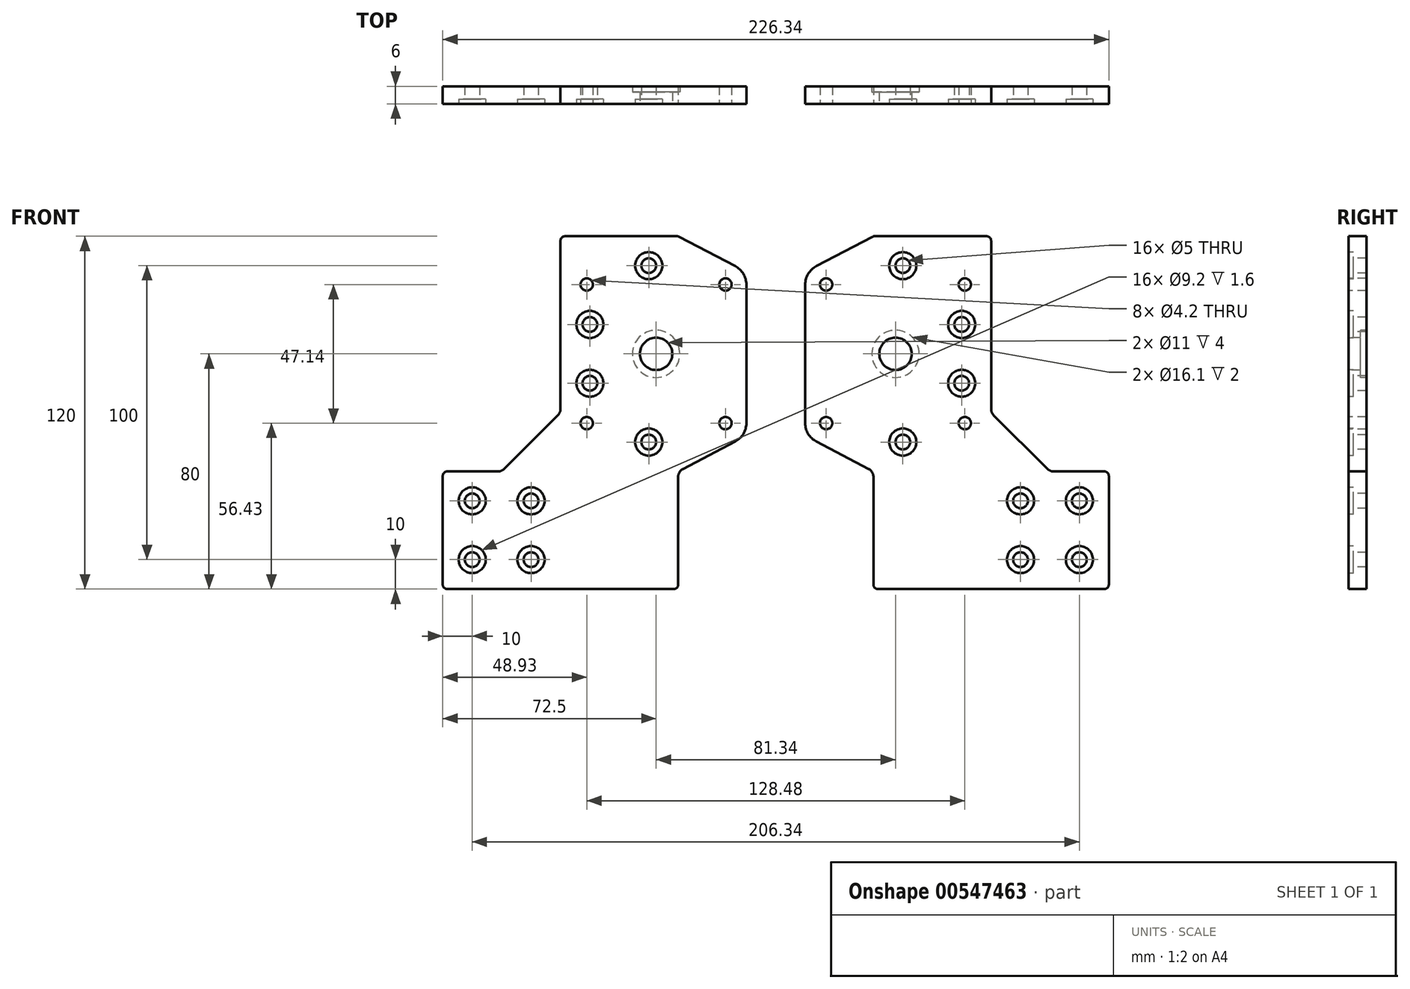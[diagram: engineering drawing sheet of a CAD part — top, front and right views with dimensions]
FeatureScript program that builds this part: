
annotation { "Feature Type Name" : "Feature", "Feature Type Description" : "" }
export const myFeature = defineFeature(function(context is Context, id is Id, definition is map)
    precondition{}
    {
        {
            var Q0;
            Q0=qCreatedBy(makeId("Front.planeOp"),FACE);
            var sketch = newSketch(context, id + "F0", { "sketchPlane" : qUnion([Q0])});
            skCircle(sketch, "E0", {"center": v(-80, -70) * mm, "radius": 2.5 * mm});
            skCircle(sketch, "E1", {"center": v(-80, -70) * mm, "radius": 4.6 * mm});
            skCircle(sketch, "E2", {"center": v(-17.5, 0) * mm, "radius": 5.5 * mm});
            skCircle(sketch, "E3", {"center": v(-17.5, 0) * mm, "radius": 8.05 * mm});
            skCircle(sketch, "E4", {"center": v(-41.07, 23.57) * mm, "radius": 2.1 * mm});
            skCircle(sketch, "E5.1.0", {"center": v(-41.07, -23.57) * mm, "radius": 2.1 * mm});
            skCircle(sketch, "E5.2.0", {"center": v(6.07, -23.57) * mm, "radius": 2.1 * mm});
            skCircle(sketch, "E5.3.0", {"center": v(6.07, 23.57) * mm, "radius": 2.1 * mm});
            skArc(sketch, "E6", {"start": v(13.17, 23.57) * mm, "mid": v(12.14, 27.25) * mm, "end": v(9.36, 29.86) * mm});
            skArc(sketch, "E7", {"start": v(9.36, -29.86) * mm, "mid": v(12.14, -27.25) * mm, "end": v(13.17, -23.57) * mm});
            skLineSegment(sketch, "E8", {"start": v(-90, -80) * mm, "end": v(-10, -80) * mm});
            skLineSegment(sketch, "E9", {"start": v(-10, -80) * mm, "end": v(-10, -40) * mm});
            skLineSegment(sketch, "E10", {"start": v(-10, -40) * mm, "end": v(9.36, -29.86) * mm});
            skLineSegment(sketch, "E11", {"start": v(-90, -80) * mm, "end": v(-90, -40) * mm});
            skLineSegment(sketch, "E12", {"start": v(-90, -40) * mm, "end": v(-70, -40) * mm});
            skLineSegment(sketch, "E13", {"start": v(-70, -40) * mm, "end": v(-50, -20) * mm});
            skLineSegment(sketch, "E14", {"start": v(-50, -20) * mm, "end": v(-50, 40) * mm});
            skLineSegment(sketch, "E15", {"start": v(-50, 40) * mm, "end": v(-10, 40) * mm});
            skLineSegment(sketch, "E16", {"start": v(-10, 40) * mm, "end": v(9.36, 29.86) * mm});
            skLineSegment(sketch, "E17", {"start": v(13.17, 23.57) * mm, "end": v(13.17, -23.57) * mm});
            skCircle(sketch, "E18.0.1.0", {"center": v(-80, -50) * mm, "radius": 4.6 * mm});
            skCircle(sketch, "E18.0.1.1", {"center": v(-80, -50) * mm, "radius": 2.5 * mm});
            skCircle(sketch, "E18.1.0.0", {"center": v(-60, -70) * mm, "radius": 4.6 * mm});
            skCircle(sketch, "E18.1.0.1", {"center": v(-60, -70) * mm, "radius": 2.5 * mm});
            skCircle(sketch, "E18.1.1.0", {"center": v(-60, -50) * mm, "radius": 4.6 * mm});
            skCircle(sketch, "E18.1.1.1", {"center": v(-60, -50) * mm, "radius": 2.5 * mm});
            skCircle(sketch, "E18.2.3.0", {"center": v(-40, -10) * mm, "radius": 4.6 * mm});
            skCircle(sketch, "E18.2.3.1", {"center": v(-40, -10) * mm, "radius": 2.5 * mm});
            skCircle(sketch, "E18.2.4.0", {"center": v(-40, 10) * mm, "radius": 4.6 * mm});
            skCircle(sketch, "E18.2.4.1", {"center": v(-40, 10) * mm, "radius": 2.5 * mm});
            skCircle(sketch, "E18.3.2.0", {"center": v(-20, -30) * mm, "radius": 4.6 * mm});
            skCircle(sketch, "E18.3.2.1", {"center": v(-20, -30) * mm, "radius": 2.5 * mm});
            skCircle(sketch, "E18.3.5.0", {"center": v(-20, 30) * mm, "radius": 4.6 * mm});
            skCircle(sketch, "E18.3.5.1", {"center": v(-20, 30) * mm, "radius": 2.5 * mm});
            skLineSegment(sketch, "E18.direction1", {"start": v(-80, -70) * mm, "end": v(-60, -70) * mm, "construction": true});
            skLineSegment(sketch, "E18.direction2", {"start": v(-80, -70) * mm, "end": v(-80, -50) * mm, "construction": true});
            skSolve(sketch);
        }
        {
            var Q0;
            Q0=makeQuery(id+"F0.imprint","IMPRINT",FACE,{"disambiguationData":[TD([[makeQuery(id+"F0.imprint","IMPRINT",EDGE,{"derivedFrom":sQuery(id+"F0.wireOp",EDGE,"E1")}),-1.0]])]});
            var Q1;
            Q1=makeQuery(id+"F0.imprint","IMPRINT",FACE,{"disambiguationData":[TD([[makeQuery(id+"F0.imprint","IMPRINT",EDGE,{"derivedFrom":sQuery(id+"F0.wireOp",EDGE,"E18.0.1.0")}),1.0]])]});
            var Q2;
            Q2=makeQuery(id+"F0.imprint","IMPRINT",FACE,{"disambiguationData":[TD([[makeQuery(id+"F0.imprint","IMPRINT",EDGE,{"derivedFrom":sQuery(id+"F0.wireOp",EDGE,"E0")}),-1.0]])]});
            var Q3;
            Q3=makeQuery(id+"F0.imprint","IMPRINT",FACE,{"disambiguationData":[TD([[makeQuery(id+"F0.imprint","IMPRINT",EDGE,{"derivedFrom":sQuery(id+"F0.wireOp",EDGE,"E18.1.1.0")}),1.0]])]});
            var Q4;
            Q4=makeQuery(id+"F0.imprint","IMPRINT",FACE,{"disambiguationData":[TD([[makeQuery(id+"F0.imprint","IMPRINT",EDGE,{"derivedFrom":sQuery(id+"F0.wireOp",EDGE,"E18.1.0.0")}),1.0]])]});
            var Q5;
            Q5=makeQuery(id+"F0.imprint","IMPRINT",FACE,{"disambiguationData":[TD([[makeQuery(id+"F0.imprint","IMPRINT",EDGE,{"derivedFrom":sQuery(id+"F0.wireOp",EDGE,"E18.3.2.0")}),1.0]])]});
            var Q6;
            Q6=makeQuery(id+"F0.imprint","IMPRINT",FACE,{"disambiguationData":[TD([[makeQuery(id+"F0.imprint","IMPRINT",EDGE,{"derivedFrom":sQuery(id+"F0.wireOp",EDGE,"E18.2.3.0")}),1.0]])]});
            var Q7;
            Q7=makeQuery(id+"F0.imprint","IMPRINT",FACE,{"disambiguationData":[TD([[makeQuery(id+"F0.imprint","IMPRINT",EDGE,{"derivedFrom":sQuery(id+"F0.wireOp",EDGE,"E2")}),-1.0]])]});
            var Q8;
            Q8=makeQuery(id+"F0.imprint","IMPRINT",FACE,{"disambiguationData":[TD([[makeQuery(id+"F0.imprint","IMPRINT",EDGE,{"derivedFrom":sQuery(id+"F0.wireOp",EDGE,"E18.2.4.0")}),1.0]])]});
            var Q9;
            Q9=makeQuery(id+"F0.imprint","IMPRINT",FACE,{"disambiguationData":[TD([[makeQuery(id+"F0.imprint","IMPRINT",EDGE,{"derivedFrom":sQuery(id+"F0.wireOp",EDGE,"E18.3.5.0")}),1.0]])]});
            extrude(context, id + "F1", {"entities" : qUnion([Q0, Q1, Q2, Q3, Q4, Q5, Q6, Q7, Q8, Q9]), "oppositeDirection" : true, "depth" : 6 * mm, "offsetDistance" : 25 * mm});
        }
        {
            var Q0;
            Q0=makeQuery(id+"F0.imprint","IMPRINT",FACE,{"disambiguationData":[TD([[makeQuery(id+"F0.imprint","IMPRINT",EDGE,{"derivedFrom":sQuery(id+"F0.wireOp",EDGE,"4f92008c-afac-4e71-bfba-3b4317ba255b.0.3.0")}),1.0]])]});
            var Q1;
            Q1=makeQuery(id+"F0.imprint","IMPRINT",FACE,{"disambiguationData":[TD([[makeQuery(id+"F0.imprint","IMPRINT",EDGE,{"derivedFrom":sQuery(id+"F0.wireOp",EDGE,"4f92008c-afac-4e71-bfba-3b4317ba255b.1.2.0")}),1.0]])]});
            var Q2;
            Q2=makeQuery(id+"F0.imprint","IMPRINT",FACE,{"disambiguationData":[TD([[makeQuery(id+"F0.imprint","IMPRINT",EDGE,{"derivedFrom":sQuery(id+"F0.wireOp",EDGE,"4f92008c-afac-4e71-bfba-3b4317ba255b.1.1.0")}),1.0]])]});
            var Q3;
            Q3=makeQuery(id+"F0.imprint","IMPRINT",FACE,{"disambiguationData":[TD([[makeQuery(id+"F0.imprint","IMPRINT",EDGE,{"derivedFrom":sQuery(id+"F0.wireOp",EDGE,"2g3J3PDK-asqC-sIAA-iO2O-egJn1byekbcv")}),-1.0]])]});
            var Q4;
            Q4=makeQuery(id+"F0.imprint","IMPRINT",FACE,{"disambiguationData":[TD([[makeQuery(id+"F0.imprint","IMPRINT",EDGE,{"derivedFrom":sQuery(id+"F0.wireOp",EDGE,"d8337e6d-cb25-4233-9b89-757700e04f83.2.1.0")}),1.0]])]});
            var Q5;
            Q5=makeQuery(id+"F0.imprint","IMPRINT",FACE,{"disambiguationData":[TD([[makeQuery(id+"F0.imprint","IMPRINT",EDGE,{"derivedFrom":sQuery(id+"F0.wireOp",EDGE,"d8337e6d-cb25-4233-9b89-757700e04f83.1.1.0")}),1.0]])]});
            var Q6;
            Q6=makeQuery(id+"F0.imprint","IMPRINT",FACE,{"disambiguationData":[TD([[makeQuery(id+"F0.imprint","IMPRINT",EDGE,{"derivedFrom":sQuery(id+"F0.wireOp",EDGE,"d8337e6d-cb25-4233-9b89-757700e04f83.0.1.0")}),1.0]])]});
            var Q7;
            Q7=makeQuery(id+"F0.imprint","IMPRINT",FACE,{"disambiguationData":[TD([[makeQuery(id+"F0.imprint","IMPRINT",EDGE,{"derivedFrom":sQuery(id+"F0.wireOp",EDGE,"E0")}),-1.0]])]});
            var Q8;
            Q8=makeQuery(id+"F0.imprint","IMPRINT",FACE,{"disambiguationData":[TD([[makeQuery(id+"F0.imprint","IMPRINT",EDGE,{"derivedFrom":sQuery(id+"F0.wireOp",EDGE,"d8337e6d-cb25-4233-9b89-757700e04f83.1.0.0")}),1.0]])]});
            var Q9;
            Q9=makeQuery(id+"F0.imprint","IMPRINT",FACE,{"disambiguationData":[TD([[makeQuery(id+"F0.imprint","IMPRINT",EDGE,{"derivedFrom":sQuery(id+"F0.wireOp",EDGE,"d8337e6d-cb25-4233-9b89-757700e04f83.2.0.0")}),1.0]])]});
            var Q10;
            Q10=makeQuery(id+"F0.imprint","IMPRINT",FACE,{"disambiguationData":[TD([[makeQuery(id+"F0.imprint","IMPRINT",EDGE,{"derivedFrom":sQuery(id+"F0.wireOp",EDGE,"E18.0.1.0")}),1.0]])]});
            var Q11;
            Q11=makeQuery(id+"F0.imprint","IMPRINT",FACE,{"disambiguationData":[TD([[makeQuery(id+"F0.imprint","IMPRINT",EDGE,{"derivedFrom":sQuery(id+"F0.wireOp",EDGE,"E18.1.1.0")}),1.0]])]});
            var Q12;
            Q12=makeQuery(id+"F0.imprint","IMPRINT",FACE,{"disambiguationData":[TD([[makeQuery(id+"F0.imprint","IMPRINT",EDGE,{"derivedFrom":sQuery(id+"F0.wireOp",EDGE,"E18.1.0.0")}),1.0]])]});
            var Q13;
            Q13=makeQuery(id+"F0.imprint","IMPRINT",FACE,{"disambiguationData":[TD([[makeQuery(id+"F0.imprint","IMPRINT",EDGE,{"derivedFrom":sQuery(id+"F0.wireOp",EDGE,"E18.3.2.0")}),1.0]])]});
            var Q14;
            Q14=makeQuery(id+"F0.imprint","IMPRINT",FACE,{"disambiguationData":[TD([[makeQuery(id+"F0.imprint","IMPRINT",EDGE,{"derivedFrom":sQuery(id+"F0.wireOp",EDGE,"E18.2.3.0")}),1.0]])]});
            var Q15;
            Q15=makeQuery(id+"F0.imprint","IMPRINT",FACE,{"disambiguationData":[TD([[makeQuery(id+"F0.imprint","IMPRINT",EDGE,{"derivedFrom":sQuery(id+"F0.wireOp",EDGE,"E18.2.4.0")}),1.0]])]});
            var Q16;
            Q16=makeQuery(id+"F0.imprint","IMPRINT",FACE,{"disambiguationData":[TD([[makeQuery(id+"F0.imprint","IMPRINT",EDGE,{"derivedFrom":sQuery(id+"F0.wireOp",EDGE,"E18.3.5.0")}),1.0]])]});
            extrude(context, id + "F2", {"entities" : qUnion([Q0, Q1, Q2, Q3, Q4, Q5, Q6, Q7, Q8, Q9, Q10, Q11, Q12, Q13, Q14, Q15, Q16]), "operationType" : NewBodyOperationType.REMOVE, "oppositeDirection" : true, "depth" : 1.6 * mm, "offsetDistance" : 25 * mm});
        }
        {
            var Q0;
            Q0=makeQuery(id+"F0.imprint","IMPRINT",FACE,{"disambiguationData":[TD([[makeQuery(id+"F0.imprint","IMPRINT",EDGE,{"derivedFrom":sQuery(id+"F0.wireOp",EDGE,"E2")}),-1.0]])]});
            extrude(context, id + "F3", {"entities" : qUnion([Q0]), "operationType" : NewBodyOperationType.REMOVE, "oppositeDirection" : true, "depth" : 6 * mm, "offsetDistance" : 25 * mm, "hasSecondDirection" : true, "secondDirectionOppositeDirection" : true, "secondDirectionDepth" : 4 * mm});
        }
        {
            var Q0;
            Q0=makeQuery(id+"F1.opExtrude","SWEPT_EDGE",EDGE,{"disambiguationData":[OSD([sQuery(id+"F0.wireOp",EDGE,"E14"),sQuery(id+"F0.wireOp",EDGE,"E15")])]});
            var Q1;
            Q1=makeQuery(id+"F1.opExtrude","SWEPT_EDGE",EDGE,{"disambiguationData":[OSD([sQuery(id+"F0.wireOp",EDGE,"E15"),sQuery(id+"F0.wireOp",EDGE,"E16")])]});
            var Q2;
            Q2=makeQuery(id+"F1.opExtrude","SWEPT_EDGE",EDGE,{"disambiguationData":[OSD([sQuery(id+"F0.wireOp",EDGE,"E11"),sQuery(id+"F0.wireOp",EDGE,"E12")])]});
            var Q3;
            Q3=makeQuery(id+"F1.opExtrude","SWEPT_EDGE",EDGE,{"disambiguationData":[OSD([sQuery(id+"F0.wireOp",EDGE,"E8"),sQuery(id+"F0.wireOp",EDGE,"E9")])]});
            var Q4;
            Q4=makeQuery(id+"F1.opExtrude","SWEPT_EDGE",EDGE,{"disambiguationData":[OSD([sQuery(id+"F0.wireOp",EDGE,"E8"),sQuery(id+"F0.wireOp",EDGE,"E11")])]});
            fillet(context, id + "F4", {"entities" : qUnion([Q0, Q1, Q2, Q3, Q4]), "radius" : 1.5 * mm, "tangentPropagation" : true, "allowEdgeOverflow" : false});
        }
        {
            var Q0;
            Q0=makeQuery(id+"F1.opExtrude","SWEPT_EDGE",EDGE,{"disambiguationData":[OSD([sQuery(id+"F0.wireOp",EDGE,"E13"),sQuery(id+"F0.wireOp",EDGE,"E14")])]});
            var Q1;
            Q1=makeQuery(id+"F1.opExtrude","SWEPT_EDGE",EDGE,{"disambiguationData":[OSD([sQuery(id+"F0.wireOp",EDGE,"E12"),sQuery(id+"F0.wireOp",EDGE,"E13")])]});
            var Q2;
            Q2=makeQuery(id+"F1.opExtrude","SWEPT_EDGE",EDGE,{"disambiguationData":[OSD([sQuery(id+"F0.wireOp",EDGE,"E9"),sQuery(id+"F0.wireOp",EDGE,"E10")])]});
            fillet(context, id + "F5", {"entities" : qUnion([Q0, Q1, Q2]), "radius" : 3 * mm, "tangentPropagation" : true, "allowEdgeOverflow" : false});
        }
        {
            var Q0;
            Q0=makeQuery(id+"F1.opExtrude","SWEPT_BODY",BODY,{"disambiguationData":[OSD([sQuery(id+"F0.wireOp",EDGE,"E0"),sQuery(id+"F0.wireOp",EDGE,"d8337e6d-cb25-4233-9b89-757700e04f83.0.1.1"),sQuery(id+"F0.wireOp",EDGE,"d8337e6d-cb25-4233-9b89-757700e04f83.1.0.1"),sQuery(id+"F0.wireOp",EDGE,"d8337e6d-cb25-4233-9b89-757700e04f83.1.1.1"),sQuery(id+"F0.wireOp",EDGE,"d8337e6d-cb25-4233-9b89-757700e04f83.2.0.1"),sQuery(id+"F0.wireOp",EDGE,"d8337e6d-cb25-4233-9b89-757700e04f83.2.1.1"),sQuery(id+"F0.wireOp",EDGE,"2g3J3PDK-asqC-sIAA-iO2O-egJn1byekbcv"),sQuery(id+"F0.wireOp",EDGE,"4f92008c-afac-4e71-bfba-3b4317ba255b.0.3.1"),sQuery(id+"F0.wireOp",EDGE,"4f92008c-afac-4e71-bfba-3b4317ba255b.1.1.1"),sQuery(id+"F0.wireOp",EDGE,"4f92008c-afac-4e71-bfba-3b4317ba255b.1.2.1"),sQuery(id+"F0.wireOp",EDGE,"E2"),sQuery(id+"F0.wireOp",EDGE,"E4"),sQuery(id+"F0.wireOp",EDGE,"E5.1.0"),sQuery(id+"F0.wireOp",EDGE,"E5.2.0"),sQuery(id+"F0.wireOp",EDGE,"E5.3.0"),sQuery(id+"F0.wireOp",EDGE,"E6"),sQuery(id+"F0.wireOp",EDGE,"E7"),sQuery(id+"F0.wireOp",EDGE,"E8"),sQuery(id+"F0.wireOp",EDGE,"E9"),sQuery(id+"F0.wireOp",EDGE,"E10"),sQuery(id+"F0.wireOp",EDGE,"E11"),sQuery(id+"F0.wireOp",EDGE,"E12"),sQuery(id+"F0.wireOp",EDGE,"E13"),sQuery(id+"F0.wireOp",EDGE,"E14"),sQuery(id+"F0.wireOp",EDGE,"E15"),sQuery(id+"F0.wireOp",EDGE,"E16"),sQuery(id+"F0.wireOp",EDGE,"E17")])]});
            var Q1;
            Q1=makeQuery(id+"F1.opExtrude","SWEPT_FACE",FACE,{"disambiguationData":[OSD([sQuery(id+"F0.wireOp",EDGE,"E17")])]});
            mirror(context, id + "F6", {"entities" : qUnion([Q0]), "mirrorPlane" : qUnion([Q1])});
        }
        {
            var Q0;
            Q0=makeQuery(id+"F6.opPattern","COPY",BODY,{"derivedFrom":makeQuery(id+"F1.opExtrude","SWEPT_BODY",BODY,{"disambiguationData":[OSD([sQuery(id+"F0.wireOp",EDGE,"E0"),sQuery(id+"F0.wireOp",EDGE,"d8337e6d-cb25-4233-9b89-757700e04f83.0.1.1"),sQuery(id+"F0.wireOp",EDGE,"d8337e6d-cb25-4233-9b89-757700e04f83.1.0.1"),sQuery(id+"F0.wireOp",EDGE,"d8337e6d-cb25-4233-9b89-757700e04f83.1.1.1"),sQuery(id+"F0.wireOp",EDGE,"d8337e6d-cb25-4233-9b89-757700e04f83.2.0.1"),sQuery(id+"F0.wireOp",EDGE,"d8337e6d-cb25-4233-9b89-757700e04f83.2.1.1"),sQuery(id+"F0.wireOp",EDGE,"2g3J3PDK-asqC-sIAA-iO2O-egJn1byekbcv"),sQuery(id+"F0.wireOp",EDGE,"4f92008c-afac-4e71-bfba-3b4317ba255b.0.3.1"),sQuery(id+"F0.wireOp",EDGE,"4f92008c-afac-4e71-bfba-3b4317ba255b.1.1.1"),sQuery(id+"F0.wireOp",EDGE,"4f92008c-afac-4e71-bfba-3b4317ba255b.1.2.1"),sQuery(id+"F0.wireOp",EDGE,"E2"),sQuery(id+"F0.wireOp",EDGE,"E4"),sQuery(id+"F0.wireOp",EDGE,"E5.1.0"),sQuery(id+"F0.wireOp",EDGE,"E5.2.0"),sQuery(id+"F0.wireOp",EDGE,"E5.3.0"),sQuery(id+"F0.wireOp",EDGE,"E6"),sQuery(id+"F0.wireOp",EDGE,"E7"),sQuery(id+"F0.wireOp",EDGE,"E8"),sQuery(id+"F0.wireOp",EDGE,"E9"),sQuery(id+"F0.wireOp",EDGE,"E10"),sQuery(id+"F0.wireOp",EDGE,"E11"),sQuery(id+"F0.wireOp",EDGE,"E12"),sQuery(id+"F0.wireOp",EDGE,"E13"),sQuery(id+"F0.wireOp",EDGE,"E14"),sQuery(id+"F0.wireOp",EDGE,"E15"),sQuery(id+"F0.wireOp",EDGE,"E16"),sQuery(id+"F0.wireOp",EDGE,"E17")])]}),"instanceName":"1"});
            transform(context, id + "F7", {"entities" : qUnion([Q0]), "transformType" : TransformType.TRANSLATION_3D, "dx" : 20 * mm, "dy" : 0 * mm, "dz" : 0 * mm, "makeCopy" : false});
        }
    });
